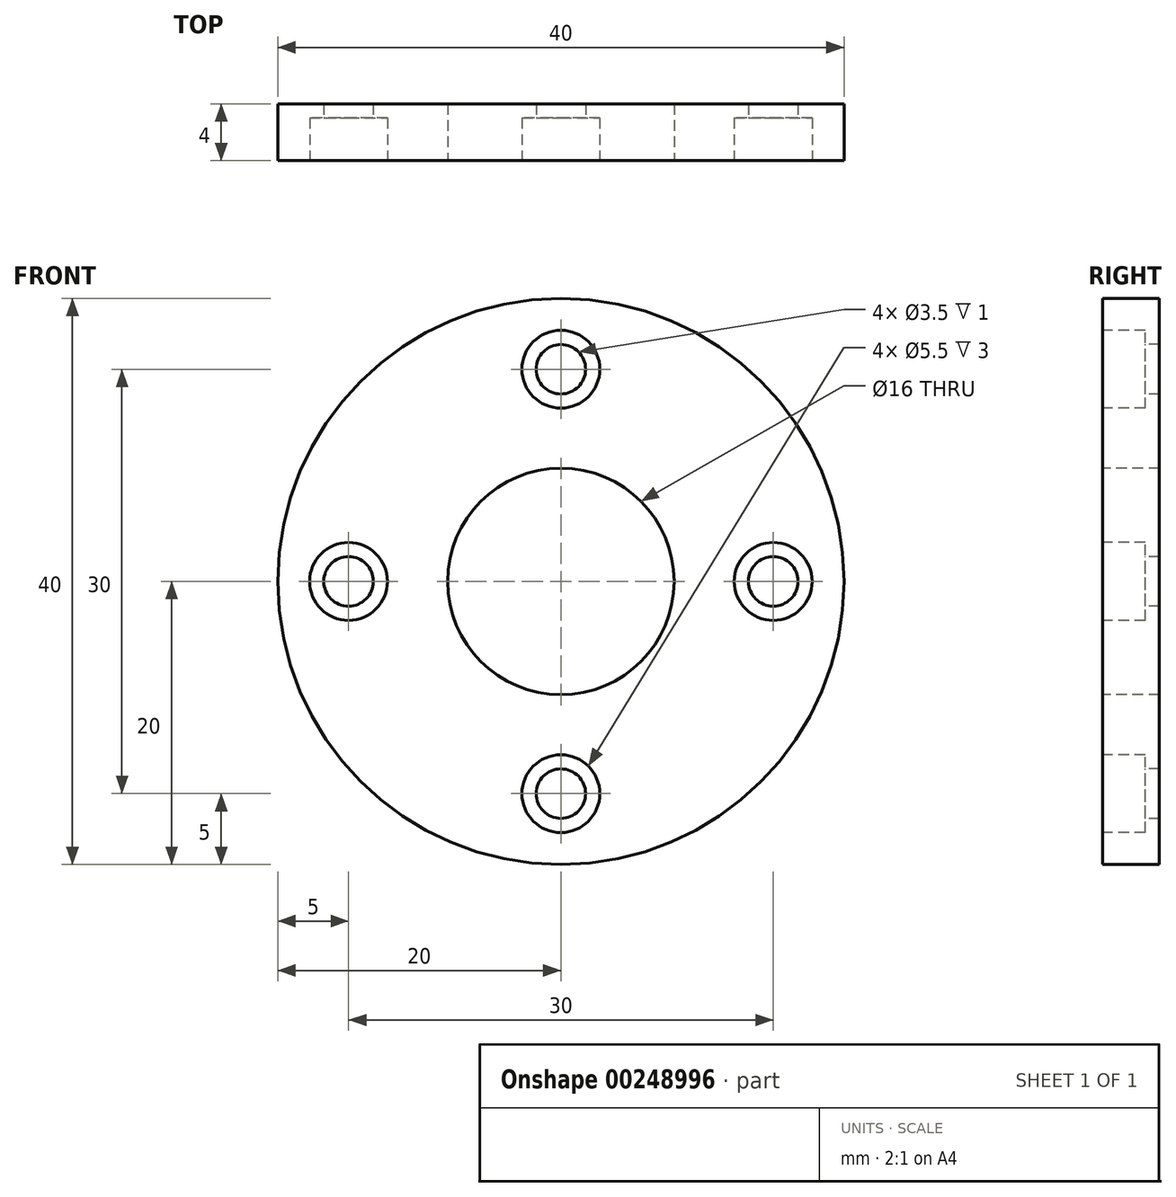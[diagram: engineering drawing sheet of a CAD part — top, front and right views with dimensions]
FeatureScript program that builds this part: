
annotation { "Feature Type Name" : "Feature", "Feature Type Description" : "" }
export const myFeature = defineFeature(function(context is Context, id is Id, definition is map)
    precondition{}
    {
        {
            var Q0;
            Q0=qCreatedBy(makeId("Front.planeOp"),FACE);
            var sketch = newSketch(context, id + "F0", { "sketchPlane" : qUnion([Q0])});
            skCircle(sketch, "E0", {"center": v(0, 0) * mm, "radius": 20 * mm});
            skPoint(sketch, "E1", {"position": v(0, 15) * mm});
            skPoint(sketch, "E2", {"position": v(-15, 0) * mm});
            skPoint(sketch, "E3", {"position": v(15, 0) * mm});
            skPoint(sketch, "E4", {"position": v(0, -15) * mm});
            skSolve(sketch);
        }
        {
            var Q0;
            Q0=makeQuery(id+"F0.imprint","IMPRINT",FACE,{"disambiguationData":[TD([[makeQuery(id+"F0.imprint","IMPRINT",EDGE,{"derivedFrom":sQuery(id+"F0.wireOp",EDGE,"E0")}),1.0]])]});
            extrude(context, id + "F1", {"entities" : qUnion([Q0]), "endBound" : BoundingType.SYMMETRIC, "depth" : 4 * mm});
        }
        {
            var Q0;
            Q0=makeQuery(id+"F1.opExtrude","CAP_FACE",FACE,{"disambiguationData":[OSD([sQuery(id+"F0.wireOp",EDGE,"E0")])],"isStart":false});
            var sketch = newSketch(context, id + "F2", { "sketchPlane" : qUnion([Q0])});
            skPoint(sketch, "E5.0", {"position": v(-15, 0) * mm});
            skPoint(sketch, "E6.0", {"position": v(0, 15) * mm});
            skPoint(sketch, "E7.0", {"position": v(15, 0) * mm});
            skPoint(sketch, "E8.0", {"position": v(0, -15) * mm});
            skPoint(sketch, "E9.0", {"position": v(0, 0) * mm});
            skSolve(sketch);
        }
        {
            var Q0;
            Q0=sQuery(id+"F2.wireOp",VERTEX,"E6.0");
            var Q1;
            Q1=sQuery(id+"F2.wireOp",VERTEX,"E5.0");
            var Q2;
            Q2=sQuery(id+"F2.wireOp",VERTEX,"E8.0");
            var Q3;
            Q3=sQuery(id+"F2.wireOp",VERTEX,"E7.0");
            var Q4;
            Q4=makeQuery(id+"F1.opExtrude","SWEPT_BODY",BODY,{"disambiguationData":[OSD([sQuery(id+"F0.wireOp",EDGE,"E0")])]});
            hole(context, id + "F3", {"style" : HoleStyle.C_BORE, "endStyle" : HoleEndStyle.THROUGH, "holeDiameter" : 3.5 * mm, "cBoreDiameter" : 5.5 * mm, "cBoreDepth" : 3 * mm, "tappedDepth" : 12 * mm, "tapClearance" : 3, "startFromSketch" : true, "locations" : qUnion([Q0, Q1, Q2, Q3]), "scope" : qUnion([Q4])});
        }
        {
            var Q0;
            Q0=sQuery(id+"F2.wireOp",VERTEX,"E9.0");
            var Q1;
            Q1=makeQuery(id+"F1.opExtrude","SWEPT_BODY",BODY,{"disambiguationData":[OSD([sQuery(id+"F0.wireOp",EDGE,"E0")])]});
            hole(context, id + "F4", {"style" : HoleStyle.SIMPLE, "endStyle" : HoleEndStyle.THROUGH, "holeDiameter" : 16 * mm, "tappedDepth" : 12 * mm, "tapClearance" : 3, "startFromSketch" : true, "locations" : qUnion([Q0]), "scope" : qUnion([Q1])});
        }
    });
